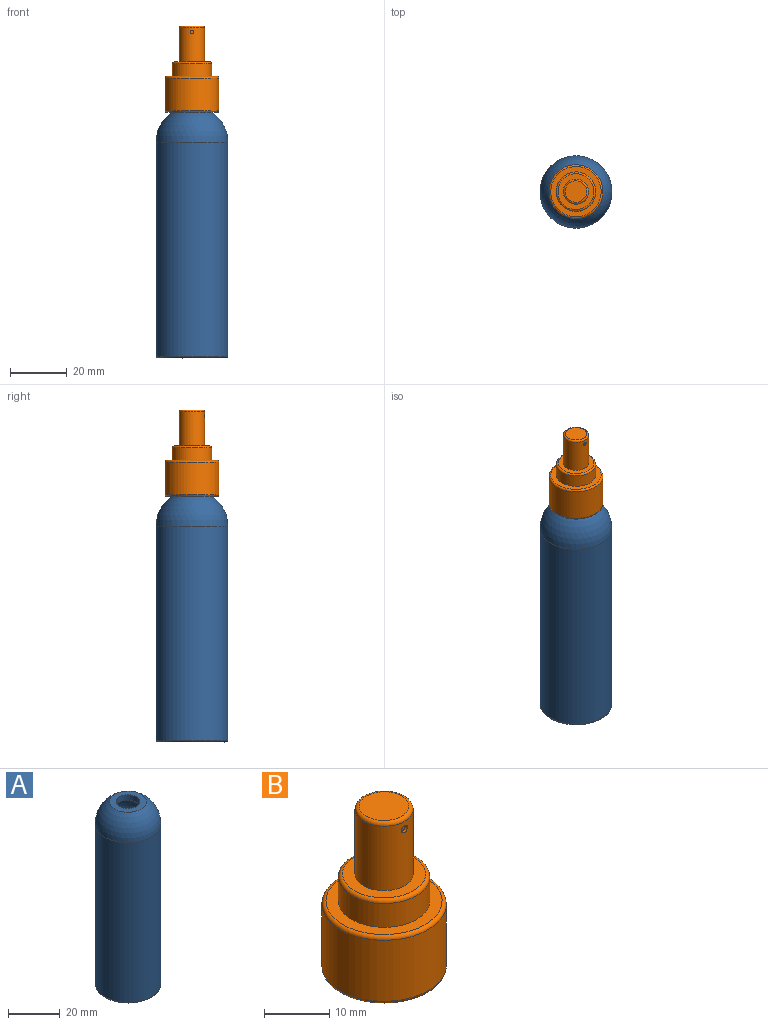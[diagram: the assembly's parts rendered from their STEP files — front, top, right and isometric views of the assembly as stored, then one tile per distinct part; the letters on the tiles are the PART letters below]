
ASSEMBLY  parts=2 mates=1
PART A: 10 faces, bbox 27.5x27.5x86.7 mm
  f0: plane 14.25x14.25mm, normal (0,0,1), area 93.4mm2, adj f1,f5
  f1: sphere r=12.7mm, area 838.9mm2, adj f0,f2
  f2: cylinder r=12.7mm len=75.57mm, axis (0,0,1), area 6029.8mm2, adj f1,f3
  f3: torus R=12.06mm, axis (0,0,1), area 78.1mm2, adj f2,f4
  f4: plane 24.13x24.13mm, normal (0,0,-1), area 457.3mm2, adj f3
  f5: cylinder r=4.58mm len=9.17mm, axis (0,0,1), area 73.2mm2, adj f0,f6
  f6: plane 12.59x12.59mm, normal (0,0,-1), area 58.5mm2, adj f5,f7
  f7: sphere r=10.16mm, area 509mm2, adj f6,f8
  f8: cylinder r=10.16mm len=73.66mm, axis (0,0,1), area 4702.2mm2, adj f7,f9
  f9: plane 20.32x20.32mm, normal (0,0,1), area 324.3mm2, adj f8
PART B: 13 faces, bbox 20.6x20.6x30.5 mm
  f0: plane 12.7x12.7mm, normal (0,0,1), area 64.6mm2, adj f1,f10
  f1: torus R=6.35mm, axis (0,0,1), area 42.3mm2, adj f0,f2
  f2: cylinder r=6.99mm len=13.97mm, axis (0,0,1), area 195.1mm2, adj f1,f3
  f3: plane 17.78x17.78mm, normal (0,0,1), area 95mm2, adj f2,f4
  f4: torus R=8.89mm, axis (0,0,1), area 58.2mm2, adj f3,f5
  f5: cylinder r=9.53mm len=19.05mm, axis (0,0,1), area 684.1mm2, adj f4,f6
  f6: torus R=8.89mm, axis (0,0,1), area 58.2mm2, adj f5,f7
  f7: plane 17.78x17.78mm, normal (0,0,-1), area 248.3mm2, adj f6
  f8: plane 7.62x7.62mm, normal (0,0,1), area 45.6mm2, adj f9
  f9: torus R=3.81mm, axis (0,0,1), area 26.4mm2, adj f8,f10
  f10: cylinder r=4.45mm len=12.07mm, axis (0,0,1), area 335.7mm2, adj f0,f9,f11
  f11: cylinder r=0.64mm len=1.27mm, axis (0,-1,0), area 1.9mm2, adj f10,f12
  f12: plane 1.27x1.27mm, normal (0,-1,0), area 1.3mm2, adj f11
PLACE A rot(axis=(0.57,-0.2,-0.79),0deg) t=(-22.56,21.25,26.08)mm
PLACE B rot(axis=(0.57,-0.2,-0.79),0deg) t=(-22.56,21.25,112.79)mm
MATE planar A.f5 <-> B.f1  axis (0,0,1) through (-22.56,21.25,112.79)mm
